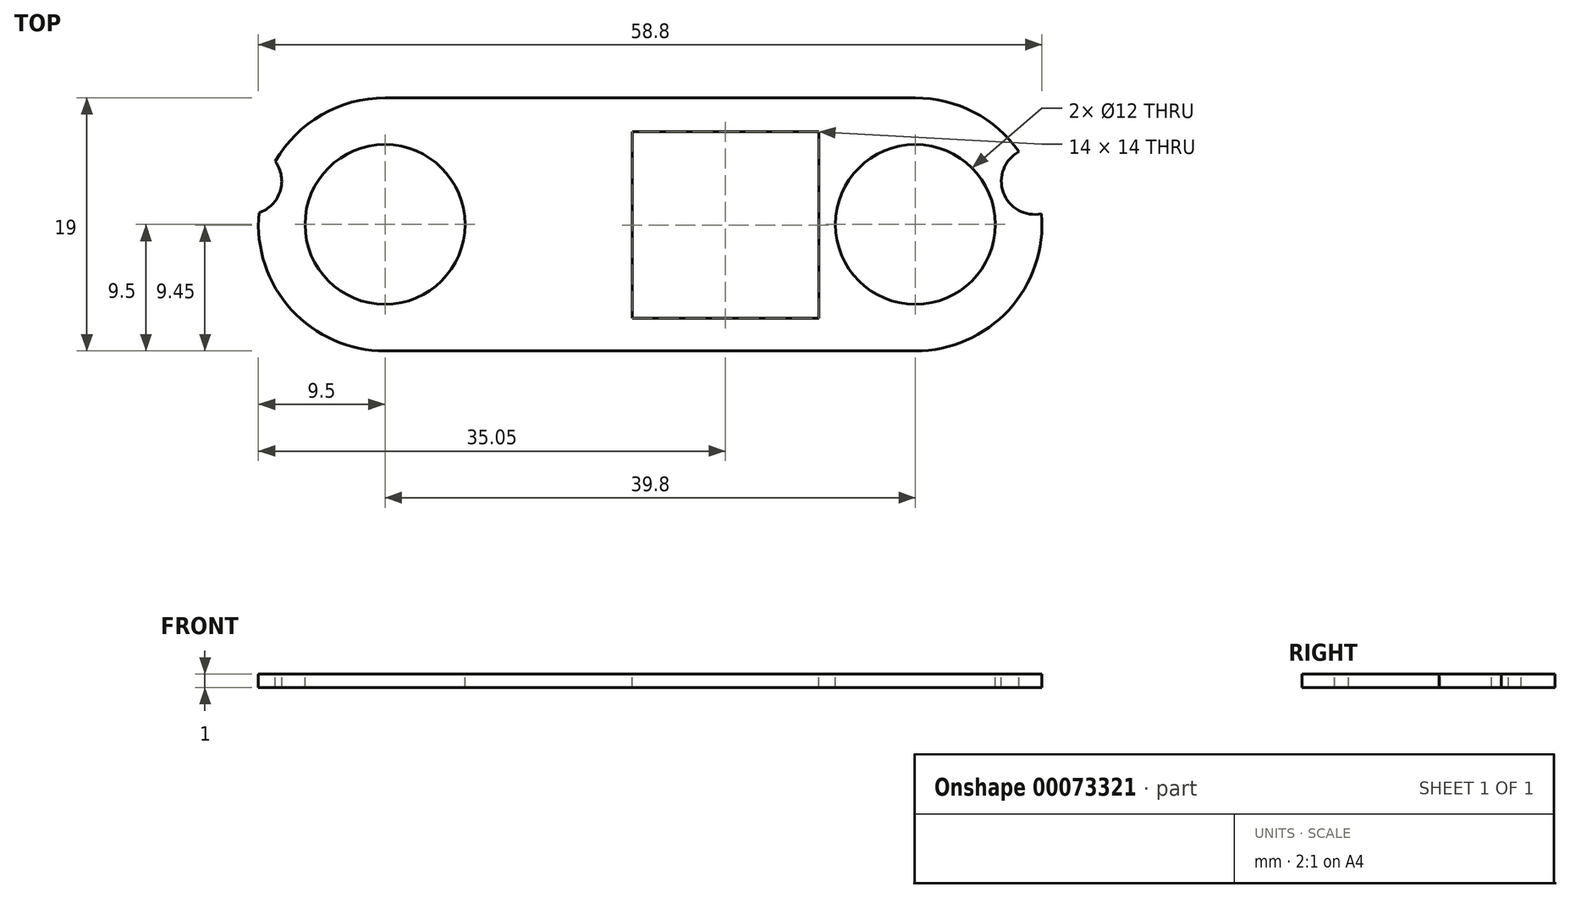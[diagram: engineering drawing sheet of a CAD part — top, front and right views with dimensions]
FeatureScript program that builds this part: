
annotation { "Feature Type Name" : "Feature", "Feature Type Description" : "" }
export const myFeature = defineFeature(function(context is Context, id is Id, definition is map)
    precondition{}
    {
        {
            var Q0;
            Q0=qCreatedBy(makeId("Top.planeOp"),FACE);
            var sketch = newSketch(context, id + "F0", { "sketchPlane" : qUnion([Q0])});
            skLineSegment(sketch, "E0.rect.bottom", {"start": v(53.6, -21.2) * mm, "end": v(-53.6, -21.2) * mm});
            skLineSegment(sketch, "E0.rect.top", {"start": v(4.1, 21.2) * mm, "end": v(-50.6, 21.2) * mm});
            skLineSegment(sketch, "E0.rect.left", {"start": v(55.6, -19.2) * mm, "end": v(55.6, -10.9) * mm});
            skLineSegment(sketch, "E0.rect.right", {"start": v(-55.6, -19.2) * mm, "end": v(-55.6, 16.2) * mm});
            skPoint(sketch, "E0.rect.middle", {"position": v(0, 0) * mm});
            skPoint(sketch, "E1.visualSharp", {"position": v(-55.6, 21.2) * mm});
            skArc(sketch, "E1.filletArc", {"start": v(-50.6, 21.2) * mm, "mid": v(-54.14, 19.74) * mm, "end": v(-55.6, 16.2) * mm});
            skPoint(sketch, "E2.visualSharp", {"position": v(-55.6, -21.2) * mm});
            skArc(sketch, "E2.filletArc", {"start": v(-55.6, -19.2) * mm, "mid": v(-55.01, -20.61) * mm, "end": v(-53.6, -21.2) * mm});
            skLineSegment(sketch, "E3.bottom", {"start": v(56.1, 1.1) * mm, "end": v(61.2, 1.1) * mm});
            skLineSegment(sketch, "E3.top", {"start": v(56.1, -10.4) * mm, "end": v(61.2, -10.4) * mm});
            skLineSegment(sketch, "E3.right", {"start": v(66.4, -2.2) * mm, "end": v(66.4, -7.1) * mm});
            skLineSegment(sketch, "E4", {"start": v(53.6, 11.9) * mm, "end": v(28.9, 11.9) * mm});
            skLineSegment(sketch, "E5", {"start": v(21.76, 13.7) * mm, "end": v(11.24, 19.4) * mm});
            skPoint(sketch, "E6.orphan", {"position": v(55.6, 21.2) * mm});
            skLineSegment(sketch, "E7.trimOffspring", {"start": v(55.6, 1.6) * mm, "end": v(55.6, 9.9) * mm});
            skPoint(sketch, "E8.visualSharp", {"position": v(55.6, 11.9) * mm});
            skArc(sketch, "E8.filletArc", {"start": v(55.6, 9.9) * mm, "mid": v(55.01, 11.31) * mm, "end": v(53.6, 11.9) * mm});
            skPoint(sketch, "E9.visualSharp", {"position": v(55.6, 1.1) * mm});
            skArc(sketch, "E9.filletArc", {"start": v(55.6, 1.6) * mm, "mid": v(55.75, 1.25) * mm, "end": v(56.1, 1.1) * mm});
            skPoint(sketch, "E10.visualSharp", {"position": v(55.6, -10.4) * mm});
            skArc(sketch, "E10.filletArc", {"start": v(56.1, -10.4) * mm, "mid": v(55.75, -10.55) * mm, "end": v(55.6, -10.9) * mm});
            skPoint(sketch, "E11.visualSharp", {"position": v(55.6, -21.2) * mm});
            skArc(sketch, "E11.filletArc", {"start": v(53.6, -21.2) * mm, "mid": v(55.01, -20.61) * mm, "end": v(55.6, -19.2) * mm});
            skArc(sketch, "E12", {"start": v(61.2, -10.4) * mm, "mid": v(64.28, -9.5) * mm, "end": v(66.4, -7.1) * mm});
            skArc(sketch, "E13.trimOffspring", {"start": v(66.4, -2.2) * mm, "mid": v(64.28, 0.2) * mm, "end": v(61.2, 1.1) * mm});
            skPoint(sketch, "E14.visualSharp", {"position": v(7.9, 21.2) * mm});
            skArc(sketch, "E14.filletArc", {"start": v(11.24, 19.4) * mm, "mid": v(7.78, 20.74) * mm, "end": v(4.1, 21.2) * mm});
            skPoint(sketch, "E15.visualSharp", {"position": v(25.1, 11.9) * mm});
            skArc(sketch, "E15.filletArc", {"start": v(21.76, 13.7) * mm, "mid": v(25.22, 12.36) * mm, "end": v(28.9, 11.9) * mm});
            skCircle(sketch, "E16", {"center": v(61.2, -4.65) * mm, "radius": 1.59 * mm});
            skCircle(sketch, "E17", {"center": v(-52.1, 17.7) * mm, "radius": 1.59 * mm});
            skCircle(sketch, "E18", {"center": v(-52.1, -17.7) * mm, "radius": 1.59 * mm});
            skLineSegment(sketch, "E19", {"start": v(53.6, 11.9) * mm, "end": v(53.6, -21.2) * mm, "construction": true});
            skLineSegment(sketch, "E20", {"start": v(61.2, -4.65) * mm, "end": v(53.6, -4.65) * mm, "construction": true});
            skLineSegment(sketch, "E21", {"start": v(-50.6, 16.2) * mm, "end": v(-55.6, 21.2) * mm, "construction": true});
            skLineSegment(sketch, "E22", {"start": v(-55.6, -21.2) * mm, "end": v(-53.6, -19.2) * mm, "construction": true});
            skSolve(sketch);
        }
        {
            var Q0;
            Q0 = qSketchRegion(id + "F0", true);
            extrude(context, id + "F1", {"entities" : qUnion([Q0]), "depth" : 1 * mm});
        }
        {
            var Q0;
            Q0=makeQuery(id+"F1.opExtrude","CAP_FACE",FACE,{"disambiguationData":[OSD([sQuery(id+"F0.wireOp",EDGE,"E0.rect.bottom"),sQuery(id+"F0.wireOp",EDGE,"E0.rect.top"),sQuery(id+"F0.wireOp",EDGE,"E0.rect.left"),sQuery(id+"F0.wireOp",EDGE,"E0.rect.right")])],"isStart":false});
            var sketch = newSketch(context, id + "F2", { "sketchPlane" : qUnion([Q0])});
            skCircle(sketch, "E23", {"center": v(-47.02, 13.84) * mm, "radius": 1.63 * mm});
            skCircle(sketch, "E24", {"center": v(-47.02, -15.16) * mm, "radius": 1.63 * mm});
            skCircle(sketch, "E25", {"center": v(-40.02, -12.66) * mm, "radius": 2 * mm});
            skCircle(sketch, "E26", {"center": v(-32.72, -12.66) * mm, "radius": 2 * mm});
            skCircle(sketch, "E27", {"center": v(-36.77, 10.59) * mm, "radius": 6 * mm});
            skCircle(sketch, "E28", {"center": v(3.03, 10.59) * mm, "radius": 6 * mm});
            skLineSegment(sketch, "E29.rect.bottom", {"start": v(-4.22, 3.54) * mm, "end": v(-18.22, 3.54) * mm});
            skLineSegment(sketch, "E29.rect.top", {"start": v(-4.22, 17.54) * mm, "end": v(-18.22, 17.54) * mm});
            skLineSegment(sketch, "E29.rect.left", {"start": v(-4.22, 3.54) * mm, "end": v(-4.22, 17.54) * mm});
            skLineSegment(sketch, "E29.rect.right", {"start": v(-18.22, 3.54) * mm, "end": v(-18.22, 17.54) * mm});
            skPoint(sketch, "E29.rect.middle", {"position": v(-11.22, 10.54) * mm});
            skLineSegment(sketch, "E30.rect.bottom", {"start": v(-6.37, -18.26) * mm, "end": v(-29.67, -18.26) * mm});
            skLineSegment(sketch, "E30.rect.top", {"start": v(-6.37, -3.46) * mm, "end": v(-29.67, -3.46) * mm});
            skLineSegment(sketch, "E30.rect.left", {"start": v(-6.37, -18.26) * mm, "end": v(-6.37, -3.46) * mm});
            skLineSegment(sketch, "E30.rect.right", {"start": v(-29.67, -18.26) * mm, "end": v(-29.67, -3.46) * mm});
            skPoint(sketch, "E30.rect.middle", {"position": v(-18.02, -10.86) * mm});
            skCircle(sketch, "E31.MirrorC", {"center": v(-2.32, -12.66) * mm, "radius": 2 * mm});
            skCircle(sketch, "E32.MirrorC", {"center": v(4.98, -12.66) * mm, "radius": 2 * mm});
            skCircle(sketch, "E33.MirrorC", {"center": v(11.98, -15.16) * mm, "radius": 1.63 * mm});
            skCircle(sketch, "E34.MirrorC", {"center": v(11.98, 13.84) * mm, "radius": 1.63 * mm});
            skPoint(sketch, "E35", {"position": v(-50.52, 17.34) * mm});
            skPoint(sketch, "E36", {"position": v(15.48, 17.34) * mm});
            skLineSegment(sketch, "E37.bottom", {"start": v(-50.52, 17.34) * mm, "end": v(15.48, 17.34) * mm, "construction": true});
            skLineSegment(sketch, "E37.top", {"start": v(-50.52, -18.66) * mm, "end": v(15.48, -18.66) * mm, "construction": true});
            skLineSegment(sketch, "E37.left", {"start": v(-50.52, 17.34) * mm, "end": v(-50.52, -18.66) * mm, "construction": true});
            skLineSegment(sketch, "E37.right", {"start": v(15.48, 17.34) * mm, "end": v(15.48, -18.66) * mm, "construction": true});
            skCircle(sketch, "E38", {"center": v(43, -4.65) * mm, "radius": 5.35 * mm});
            skLineSegment(sketch, "E39.bottom", {"start": v(31.98, -14.55) * mm, "end": v(18.98, -14.55) * mm});
            skLineSegment(sketch, "E39.top", {"start": v(31.98, 5.25) * mm, "end": v(18.98, 5.25) * mm});
            skLineSegment(sketch, "E39.left", {"start": v(31.98, -14.55) * mm, "end": v(31.98, 5.25) * mm});
            skLineSegment(sketch, "E39.right", {"start": v(18.98, -14.55) * mm, "end": v(18.98, 5.25) * mm});
            skPoint(sketch, "E39.middle", {"position": v(25.48, -4.65) * mm});
            skLineSegment(sketch, "E40", {"start": v(61.2, -4.65) * mm, "end": v(15.48, -4.65) * mm});
            skSolve(sketch);
        }
        {
            var Q0;
            Q0 = qSketchRegion(id + "F2", true);
            extrude(context, id + "F3", {"entities" : qUnion([Q0]), "operationType" : NewBodyOperationType.REMOVE, "endBound" : BoundingType.THROUGH_ALL, "oppositeDirection" : true, "depth" : 25 * mm});
        }
        {
            var Q0;
            Q0=makeQuery(id+"F1.opExtrude","CAP_FACE",FACE,{"disambiguationData":[OSD([sQuery(id+"F0.wireOp",EDGE,"E0.rect.bottom"),sQuery(id+"F0.wireOp",EDGE,"E0.rect.top"),sQuery(id+"F0.wireOp",EDGE,"E0.rect.left"),sQuery(id+"F0.wireOp",EDGE,"E0.rect.right"),sQuery(id+"F0.wireOp",EDGE,"E1.filletArc"),sQuery(id+"F0.wireOp",EDGE,"E2.filletArc"),sQuery(id+"F0.wireOp",EDGE,"E3.bottom"),sQuery(id+"F0.wireOp",EDGE,"E3.top"),sQuery(id+"F0.wireOp",EDGE,"E3.right"),sQuery(id+"F0.wireOp",EDGE,"E4"),sQuery(id+"F0.wireOp",EDGE,"E5"),sQuery(id+"F0.wireOp",EDGE,"E7.trimOffspring"),sQuery(id+"F0.wireOp",EDGE,"E8.filletArc"),sQuery(id+"F0.wireOp",EDGE,"E9.filletArc"),sQuery(id+"F0.wireOp",EDGE,"E10.filletArc"),sQuery(id+"F0.wireOp",EDGE,"E11.filletArc"),sQuery(id+"F0.wireOp",EDGE,"E12"),sQuery(id+"F0.wireOp",EDGE,"E13.trimOffspring"),sQuery(id+"F0.wireOp",EDGE,"E14.filletArc"),sQuery(id+"F0.wireOp",EDGE,"E15.filletArc"),sQuery(id+"F0.wireOp",EDGE,"E16"),sQuery(id+"F0.wireOp",EDGE,"E17"),sQuery(id+"F0.wireOp",EDGE,"E18")])],"isStart":false});
            var sketch = newSketch(context, id + "F4", { "sketchPlane" : qUnion([Q0])});
            skLineSegment(sketch, "E41.0", {"start": v(53.1, -18.7) * mm, "end": v(53.1, -10.9) * mm});
            skLineSegment(sketch, "E41.1", {"start": v(53.1, -18.7) * mm, "end": v(-47.1, -18.7) * mm});
            skLineSegment(sketch, "E41.2", {"start": v(-52.1, -13.7) * mm, "end": v(-52.1, 13.7) * mm});
            skLineSegment(sketch, "E41.3", {"start": v(4.1, 18.7) * mm, "end": v(-47.1, 18.7) * mm});
            skArc(sketch, "E41.4", {"start": v(10.05, 17.2) * mm, "mid": v(7.17, 18.32) * mm, "end": v(4.1, 18.7) * mm});
            skLineSegment(sketch, "E41.5", {"start": v(53.1, 1.6) * mm, "end": v(53.1, 9.4) * mm});
            skLineSegment(sketch, "E41.6", {"start": v(53.1, 9.4) * mm, "end": v(28.9, 9.4) * mm});
            skArc(sketch, "E41.7", {"start": v(20.57, 11.5) * mm, "mid": v(24.6, 9.93) * mm, "end": v(28.9, 9.4) * mm});
            skLineSegment(sketch, "E41.8", {"start": v(20.57, 11.5) * mm, "end": v(10.05, 17.2) * mm});
            skLineSegment(sketch, "E42", {"start": v(53.1, 1.6) * mm, "end": v(53.1, -10.9) * mm});
            skPoint(sketch, "E43.visualSharp", {"position": v(-52.1, 18.7) * mm});
            skArc(sketch, "E43.filletArc", {"start": v(-47.1, 18.7) * mm, "mid": v(-50.64, 17.24) * mm, "end": v(-52.1, 13.7) * mm});
            skPoint(sketch, "E44.visualSharp", {"position": v(-52.1, -18.7) * mm});
            skArc(sketch, "E44.filletArc", {"start": v(-52.1, -13.7) * mm, "mid": v(-50.64, -17.24) * mm, "end": v(-47.1, -18.7) * mm});
            skSolve(sketch);
        }
        {
            var Q0;
            Q0=makeQuery(id+"F1.opExtrude","CAP_FACE",FACE,{"disambiguationData":[OSD([sQuery(id+"F0.wireOp",EDGE,"E0.rect.bottom"),sQuery(id+"F0.wireOp",EDGE,"E0.rect.top"),sQuery(id+"F0.wireOp",EDGE,"E0.rect.left"),sQuery(id+"F0.wireOp",EDGE,"E0.rect.right"),sQuery(id+"F0.wireOp",EDGE,"E1.filletArc"),sQuery(id+"F0.wireOp",EDGE,"E2.filletArc"),sQuery(id+"F0.wireOp",EDGE,"E3.bottom"),sQuery(id+"F0.wireOp",EDGE,"E3.top"),sQuery(id+"F0.wireOp",EDGE,"E3.right"),sQuery(id+"F0.wireOp",EDGE,"E4"),sQuery(id+"F0.wireOp",EDGE,"E5"),sQuery(id+"F0.wireOp",EDGE,"E7.trimOffspring"),sQuery(id+"F0.wireOp",EDGE,"E8.filletArc"),sQuery(id+"F0.wireOp",EDGE,"E9.filletArc"),sQuery(id+"F0.wireOp",EDGE,"E10.filletArc"),sQuery(id+"F0.wireOp",EDGE,"E11.filletArc"),sQuery(id+"F0.wireOp",EDGE,"E12"),sQuery(id+"F0.wireOp",EDGE,"E13.trimOffspring"),sQuery(id+"F0.wireOp",EDGE,"E14.filletArc"),sQuery(id+"F0.wireOp",EDGE,"E15.filletArc"),sQuery(id+"F0.wireOp",EDGE,"E16"),sQuery(id+"F0.wireOp",EDGE,"E17"),sQuery(id+"F0.wireOp",EDGE,"E18")])],"isStart":false});
            var sketch = newSketch(context, id + "F5", { "sketchPlane" : qUnion([Q0])});
            skLineSegment(sketch, "E45.bottom", {"start": v(55.6, 1.6) * mm, "end": v(66.4, 1.6) * mm});
            skLineSegment(sketch, "E45.top", {"start": v(55.6, -10.9) * mm, "end": v(66.4, -10.9) * mm});
            skLineSegment(sketch, "E45.left", {"start": v(55.6, 1.6) * mm, "end": v(55.6, -10.9) * mm});
            skLineSegment(sketch, "E45.right", {"start": v(66.4, 1.6) * mm, "end": v(66.4, -10.9) * mm});
            skSolve(sketch);
        }
        {
            var Q0;
            Q0=makeQuery(id+"F1.opExtrude","CAP_FACE",FACE,{"disambiguationData":[OSD([sQuery(id+"F0.wireOp",EDGE,"E0.rect.bottom"),sQuery(id+"F0.wireOp",EDGE,"E0.rect.top"),sQuery(id+"F0.wireOp",EDGE,"E0.rect.left"),sQuery(id+"F0.wireOp",EDGE,"E0.rect.right"),sQuery(id+"F0.wireOp",EDGE,"E1.filletArc"),sQuery(id+"F0.wireOp",EDGE,"E2.filletArc"),sQuery(id+"F0.wireOp",EDGE,"E3.bottom"),sQuery(id+"F0.wireOp",EDGE,"E3.top"),sQuery(id+"F0.wireOp",EDGE,"E3.right"),sQuery(id+"F0.wireOp",EDGE,"E4"),sQuery(id+"F0.wireOp",EDGE,"E5"),sQuery(id+"F0.wireOp",EDGE,"E7.trimOffspring"),sQuery(id+"F0.wireOp",EDGE,"E8.filletArc"),sQuery(id+"F0.wireOp",EDGE,"E9.filletArc"),sQuery(id+"F0.wireOp",EDGE,"E10.filletArc"),sQuery(id+"F0.wireOp",EDGE,"E11.filletArc"),sQuery(id+"F0.wireOp",EDGE,"E12"),sQuery(id+"F0.wireOp",EDGE,"E13.trimOffspring"),sQuery(id+"F0.wireOp",EDGE,"E14.filletArc"),sQuery(id+"F0.wireOp",EDGE,"E15.filletArc"),sQuery(id+"F0.wireOp",EDGE,"E16"),sQuery(id+"F0.wireOp",EDGE,"E17"),sQuery(id+"F0.wireOp",EDGE,"E18")])],"isStart":false});
            var sketch = newSketch(context, id + "F6", { "sketchPlane" : qUnion([Q0])});
            skArc(sketch, "E46", {"start": v(-36.77, 20.09) * mm, "mid": v(-41.53, 18.81) * mm, "end": v(-45, 15.32) * mm});
            skArc(sketch, "E47", {"start": v(3.03, 1.09) * mm, "mid": v(10.03, 4.16) * mm, "end": v(12.5, 11.4) * mm});
            skLineSegment(sketch, "E48", {"start": v(-36.77, 20.09) * mm, "end": v(3.03, 20.09) * mm});
            skLineSegment(sketch, "E49", {"start": v(3.03, 1.09) * mm, "end": v(-36.77, 1.09) * mm});
            skArc(sketch, "E50", {"start": v(-46.23, 11.47) * mm, "mid": v(-44.64, 13.08) * mm, "end": v(-45, 15.32) * mm});
            skArc(sketch, "E51", {"start": v(10.8, 16.05) * mm, "mid": v(9.63, 12.99) * mm, "end": v(12.5, 11.4) * mm});
            skArc(sketch, "E52.trimOffspring", {"start": v(-46.23, 11.47) * mm, "mid": v(-43.8, 4.2) * mm, "end": v(-36.77, 1.09) * mm});
            skArc(sketch, "E53.trimOffspring", {"start": v(10.8, 16.05) * mm, "mid": v(7.41, 19.02) * mm, "end": v(3.03, 20.09) * mm});
            skSolve(sketch);
        }
        {
            var Q0;
            Q0 = qSketchRegion(id + "F6", true);
            extrude(context, id + "F7", {"entities" : qUnion([Q0]), "operationType" : NewBodyOperationType.INTERSECT, "endBound" : BoundingType.THROUGH_ALL, "oppositeDirection" : true, "depth" : 25 * mm});
        }
    });
